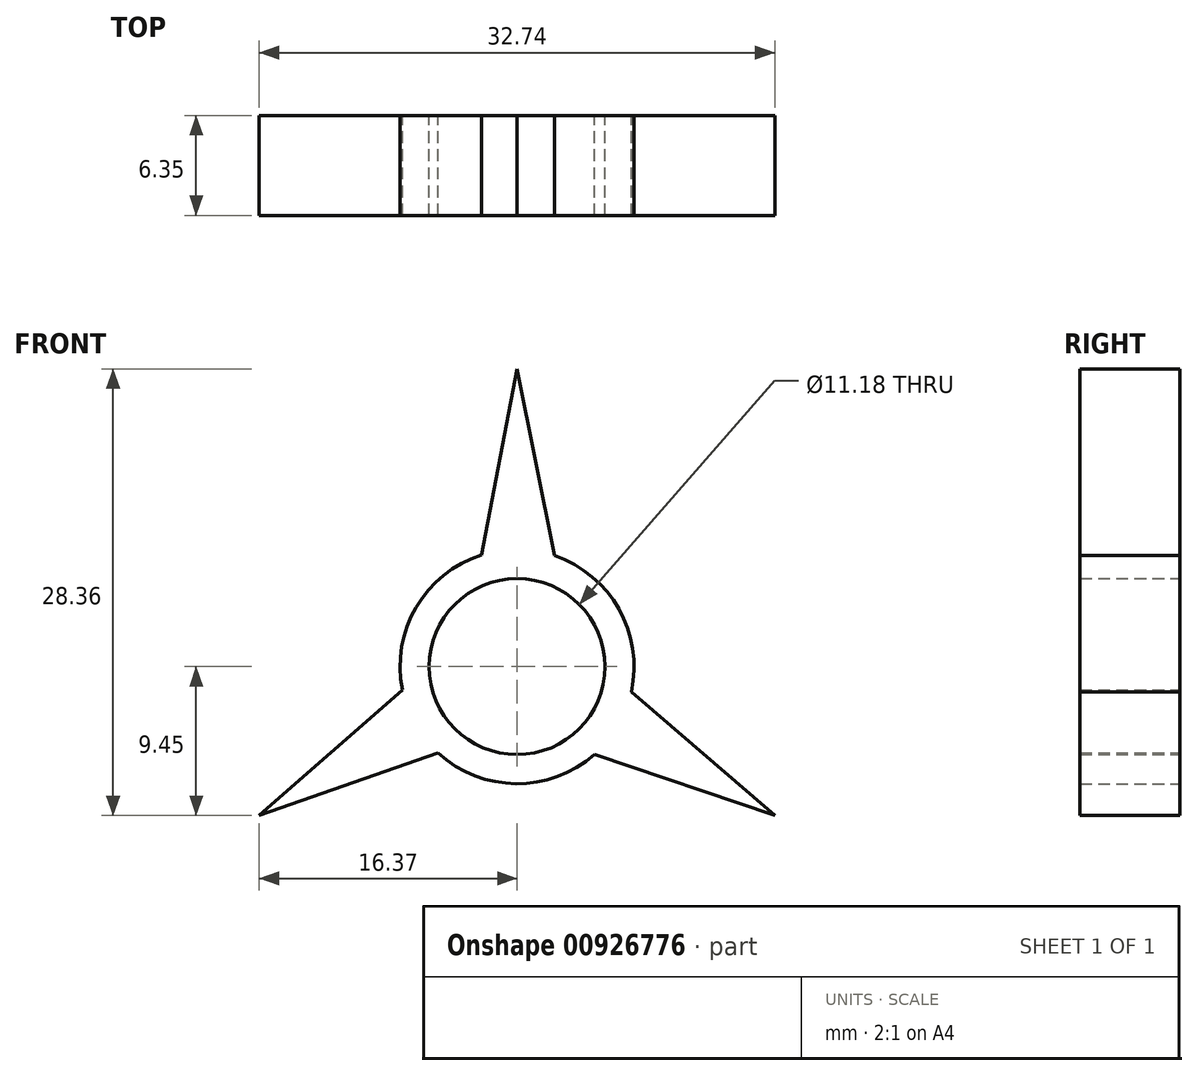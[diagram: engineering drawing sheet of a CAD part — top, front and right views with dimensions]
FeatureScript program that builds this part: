
annotation { "Feature Type Name" : "Feature", "Feature Type Description" : "" }
export const myFeature = defineFeature(function(context is Context, id is Id, definition is map)
    precondition{}
    {
        {
            var Q0;
            Q0=qCreatedBy(makeId("Front.planeOp"),FACE);
            var sketch = newSketch(context, id + "F0", { "sketchPlane" : qUnion([Q0])});
            skLineSegment(sketch, "E0", {"start": v(0, 0) * mm, "end": v(0, 5.06) * mm});
            skLineSegment(sketch, "E1", {"start": v(0, 0) * mm, "end": v(2.96, 4.05) * mm});
            skLineSegment(sketch, "E2", {"start": v(0, 0) * mm, "end": v(-2.83, 4) * mm});
            skLineSegment(sketch, "E3", {"start": v(-2.83, 4) * mm, "end": v(0, 18.9) * mm});
            skLineSegment(sketch, "E4", {"start": v(2.96, 4.05) * mm, "end": v(0, 18.9) * mm});
            skLineSegment(sketch, "E5.1.0", {"start": v(-5, 0.54) * mm, "end": v(-16.37, -9.45) * mm});
            skLineSegment(sketch, "E5.1.1", {"start": v(0, 0) * mm, "end": v(-2.06, -4.46) * mm});
            skLineSegment(sketch, "E5.1.2", {"start": v(0, 0) * mm, "end": v(-5, 0.54) * mm});
            skLineSegment(sketch, "E5.1.3", {"start": v(-2.06, -4.46) * mm, "end": v(-16.37, -9.45) * mm});
            skLineSegment(sketch, "E5.1.4", {"start": v(0, 0) * mm, "end": v(-4.38, -2.53) * mm});
            skLineSegment(sketch, "E5.2.0", {"start": v(2.03, -4.6) * mm, "end": v(16.37, -9.45) * mm});
            skLineSegment(sketch, "E5.2.1", {"start": v(0, 0) * mm, "end": v(4.89, 0.45) * mm});
            skLineSegment(sketch, "E5.2.2", {"start": v(0, 0) * mm, "end": v(2.03, -4.6) * mm});
            skLineSegment(sketch, "E5.2.3", {"start": v(4.89, 0.45) * mm, "end": v(16.37, -9.45) * mm});
            skLineSegment(sketch, "E5.2.4", {"start": v(0, 0) * mm, "end": v(4.38, -2.53) * mm});
            skPoint(sketch, "E5.center", {"position": v(0, 0) * mm});
            skCircle(sketch, "E6", {"center": v(0, 0) * mm, "radius": 7.44 * mm});
            skCircle(sketch, "E7", {"center": v(0, 0) * mm, "radius": 5.59 * mm});
            skSolve(sketch);
        }
        {
            var Q0;
            {var subQ0=sQuery(id+"F0.wireOp",EDGE,"E6");var subQ1=sQuery(id+"F0.wireOp",EDGE,"E3");var subQ2=makeQuery(id+"F0.imprint","INTERSECT",VERTEX,{"derivedFrom":[subQ1,subQ0]});Q0=makeQuery(id+"F0.imprint","IMPRINT",FACE,{"disambiguationData":[TD([[makeQuery(id+"F0.imprint","IMPRINT",EDGE,{"disambiguationData":[TD([[subQ2,1.0]])],"derivedFrom":subQ1}),1.0]])]});}
            var Q1;
            {var subQ0=sQuery(id+"F0.wireOp",EDGE,"E6");var subQ1=sQuery(id+"F0.wireOp",EDGE,"E3");var subQ2=makeQuery(id+"F0.imprint","INTERSECT",VERTEX,{"derivedFrom":[subQ1,subQ0]});Q1=makeQuery(id+"F0.imprint","IMPRINT",FACE,{"disambiguationData":[TD([[makeQuery(id+"F0.imprint","IMPRINT",EDGE,{"disambiguationData":[TD([[subQ2,1.0]])],"derivedFrom":subQ1}),-1.0]])]});}
            var Q2;
            {var subQ0=sQuery(id+"F0.wireOp",EDGE,"E6");var subQ1=sQuery(id+"F0.wireOp",EDGE,"E4");var subQ2=makeQuery(id+"F0.imprint","INTERSECT",VERTEX,{"derivedFrom":[subQ1,subQ0]});Q2=makeQuery(id+"F0.imprint","IMPRINT",FACE,{"disambiguationData":[TD([[makeQuery(id+"F0.imprint","IMPRINT",EDGE,{"disambiguationData":[TD([[subQ2,1.0]])],"derivedFrom":subQ1}),-1.0]])]});}
            var Q3;
            {var subQ0=sQuery(id+"F0.wireOp",EDGE,"E4");var subQ1=sQuery(id+"F0.wireOp",EDGE,"E3");var subQ2=makeQuery(id+"F0.imprint","INTERSECT",VERTEX,{"derivedFrom":[subQ1,subQ0]});Q3=makeQuery(id+"F0.imprint","IMPRINT",FACE,{"disambiguationData":[TD([[makeQuery(id+"F0.imprint","IMPRINT",EDGE,{"disambiguationData":[TD([[subQ2,1.0]])],"derivedFrom":subQ1}),-1.0]])]});}
            var Q4;
            {var subQ0=sQuery(id+"F0.wireOp",EDGE,"E5.2.3");var subQ1=sQuery(id+"F0.wireOp",EDGE,"E5.2.0");var subQ2=makeQuery(id+"F0.imprint","INTERSECT",VERTEX,{"derivedFrom":[subQ1,subQ0]});Q4=makeQuery(id+"F0.imprint","IMPRINT",FACE,{"disambiguationData":[TD([[makeQuery(id+"F0.imprint","IMPRINT",EDGE,{"disambiguationData":[TD([[subQ2,1.0]])],"derivedFrom":subQ1}),1.0]])]});}
            var Q5;
            {var subQ0=sQuery(id+"F0.wireOp",EDGE,"E6");var subQ1=sQuery(id+"F0.wireOp",EDGE,"E5.2.0");var subQ2=makeQuery(id+"F0.imprint","INTERSECT",VERTEX,{"derivedFrom":[subQ1,subQ0]});Q5=makeQuery(id+"F0.imprint","IMPRINT",FACE,{"disambiguationData":[TD([[makeQuery(id+"F0.imprint","IMPRINT",EDGE,{"disambiguationData":[TD([[subQ2,1.0]])],"derivedFrom":subQ1}),1.0]])]});}
            var Q6;
            {var subQ0=sQuery(id+"F0.wireOp",EDGE,"E6");var subQ1=sQuery(id+"F0.wireOp",EDGE,"E5.1.3");var subQ2=makeQuery(id+"F0.imprint","INTERSECT",VERTEX,{"derivedFrom":[subQ1,subQ0]});Q6=makeQuery(id+"F0.imprint","IMPRINT",FACE,{"disambiguationData":[TD([[makeQuery(id+"F0.imprint","IMPRINT",EDGE,{"disambiguationData":[TD([[subQ2,1.0]])],"derivedFrom":subQ1}),1.0]])]});}
            var Q7;
            {var subQ0=sQuery(id+"F0.wireOp",EDGE,"E5.1.3");var subQ1=sQuery(id+"F0.wireOp",EDGE,"E5.1.0");var subQ2=makeQuery(id+"F0.imprint","INTERSECT",VERTEX,{"derivedFrom":[subQ1,subQ0]});Q7=makeQuery(id+"F0.imprint","IMPRINT",FACE,{"disambiguationData":[TD([[makeQuery(id+"F0.imprint","IMPRINT",EDGE,{"disambiguationData":[TD([[subQ2,1.0]])],"derivedFrom":subQ1}),1.0]])]});}
            var Q8;
            {var subQ0=sQuery(id+"F0.wireOp",EDGE,"E6");var subQ1=sQuery(id+"F0.wireOp",EDGE,"E5.1.0");var subQ2=makeQuery(id+"F0.imprint","INTERSECT",VERTEX,{"derivedFrom":[subQ1,subQ0]});Q8=makeQuery(id+"F0.imprint","IMPRINT",FACE,{"disambiguationData":[TD([[makeQuery(id+"F0.imprint","IMPRINT",EDGE,{"disambiguationData":[TD([[subQ2,1.0]])],"derivedFrom":subQ1}),1.0]])]});}
            extrude(context, id + "F1", {"entities" : qUnion([Q0, Q1, Q2, Q3, Q4, Q5, Q6, Q7, Q8]), "depth" : 6.35 * mm, "offsetDistance" : 25.4 * mm});
        }
    });
